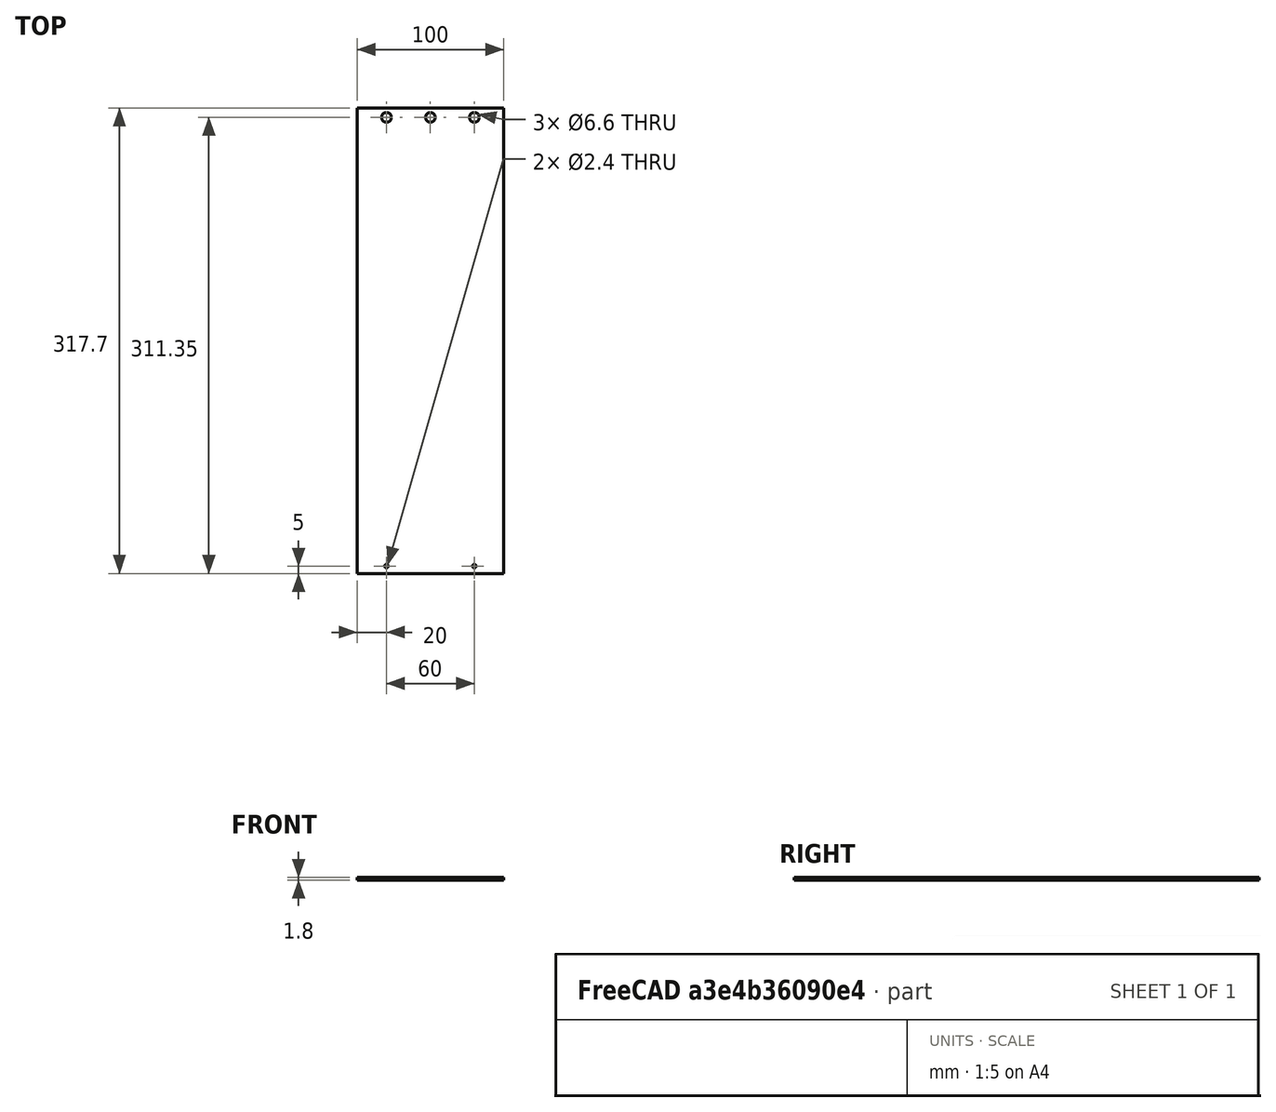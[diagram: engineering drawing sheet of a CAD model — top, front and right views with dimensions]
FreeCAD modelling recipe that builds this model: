
FCSTD DOCUMENT  (FreeCAD 0.20R29603 (Git))
Label: MechanicalCF35Mount004
License: All rights reserved
LicenseURL: http://en.wikipedia.org/wiki/All_rights_reserved
objects: Part::Cylinder×14, Part::Compound×10, TechDraw::DrawViewDimension×8, TechDraw::DrawProjGroupItem×2, Part::Box×1, Part::Cut×1, Part::Feature×1, TechDraw::DrawSVGTemplate×1, TechDraw::DrawProjGroup×1, TechDraw::DrawPage×1
note: 27 computed .brp shape members not serialized (recipe doc carries the construction recipe); baked Part::Feature solids carry a one-line shape summary decoded from their .brp

FEATURE [Part::Box] Box  label="Würfel"
  AttacherType = Attacher::AttachEngine3D
  Height = 1.8
  Length = 100
  Placement = pos=(-50,-305,50) rot=(0,0,1;0rad)
  Width = 317.7
FEATURE [Part::Cylinder] Cylinder  label="Zylinder"
  Angle = 360
  AttacherType = Attacher::AttachEngine3D
  FirstAngle = 0
  Height = 20
  Placement = pos=(30,2,40) rot=(0,0,1;0rad)
  Radius = 1.2
  SecondAngle = 0
FEATURE [Part::Cylinder] Cylinder015  label="Zylinder015"
  Angle = 360
  AttacherType = Attacher::AttachEngine3D
  FirstAngle = 0
  Height = 20
  Placement = pos=(-30,2,40) rot=(0,0,1;0rad)
  Radius = 1.2
  SecondAngle = 0
FEATURE [Part::Compound] Compound
  Links = -> [Cylinder,Cylinder015]
FEATURE [Part::Cylinder] Cylinder016  label="Zylinder016"
  Angle = 360
  AttacherType = Attacher::AttachEngine3D
  FirstAngle = 0
  Height = 20
  Placement = pos=(30,2,40) rot=(0,0,1;0rad)
  Radius = 1.2
  SecondAngle = 0
FEATURE [Part::Cylinder] Cylinder017  label="Zylinder017"
  Angle = 360
  AttacherType = Attacher::AttachEngine3D
  FirstAngle = 0
  Height = 20
  Placement = pos=(-30,2,40) rot=(0,0,1;0rad)
  Radius = 1.2
  SecondAngle = 0
FEATURE [Part::Compound] Compound015
  Links = -> [Cylinder016,Cylinder017]
  Placement = pos=(0,0,0) rot=(0,1,0;1.5708rad)
FEATURE [Part::Cylinder] Cylinder018  label="Zylinder018"
  Angle = 360
  AttacherType = Attacher::AttachEngine3D
  FirstAngle = 0
  Height = 20
  Placement = pos=(30,2,40) rot=(0,0,1;0rad)
  Radius = 1.2
  SecondAngle = 0
FEATURE [Part::Cylinder] Cylinder019  label="Zylinder019"
  Angle = 360
  AttacherType = Attacher::AttachEngine3D
  FirstAngle = 0
  Height = 20
  Placement = pos=(-30,2,40) rot=(0,0,1;0rad)
  Radius = 1.2
  SecondAngle = 0
FEATURE [Part::Compound] Compound016
  Links = -> [Cylinder018,Cylinder019]
  Placement = pos=(0,0,0) rot=(0,1,0;3.14159rad)
FEATURE [Part::Cylinder] Cylinder020  label="Zylinder020"
  Angle = 360
  AttacherType = Attacher::AttachEngine3D
  FirstAngle = 0
  Height = 20
  Placement = pos=(30,2,40) rot=(0,0,1;0rad)
  Radius = 1.2
  SecondAngle = 0
FEATURE [Part::Cylinder] Cylinder021  label="Zylinder021"
  Angle = 360
  AttacherType = Attacher::AttachEngine3D
  FirstAngle = 0
  Height = 20
  Placement = pos=(-30,2,40) rot=(0,0,1;0rad)
  Radius = 1.2
  SecondAngle = 0
FEATURE [Part::Compound] Compound017
  Links = -> [Cylinder020,Cylinder021]
  Placement = pos=(0,0,0) rot=(0,-1,0;1.5708rad)
FEATURE [Part::Compound] Compound018  label="M2Corehole"
  Links = -> [Compound017,Compound,Compound015,Compound016]
  Placement = pos=(0,-302,0) rot=(0,0,1;0rad)
FEATURE [Part::Cylinder] Cylinder004  label="Zylinder004"
  Angle = 360
  AttacherType = Attacher::AttachEngine3D
  FirstAngle = 0
  Height = 200
  Placement = pos=(30,6.35,-100) rot=(0,0,1;0rad)
  Radius = 3.3
  SecondAngle = 0
FEATURE [Part::Cylinder] Cylinder005  label="Zylinder005"
  Angle = 360
  AttacherType = Attacher::AttachEngine3D
  FirstAngle = 0
  Height = 200
  Placement = pos=(-30,6.35,-100) rot=(0,0,1;0rad)
  Radius = 3.3
  SecondAngle = 0
FEATURE [Part::Cylinder] Cylinder006  label="Zylinder006"
  Angle = 360
  AttacherType = Attacher::AttachEngine3D
  FirstAngle = 0
  Height = 200
  Placement = pos=(-30,6.35,-100) rot=(0,0,1;0rad)
  Radius = 3.3
  SecondAngle = 0
FEATURE [Part::Cylinder] Cylinder007  label="Zylinder007"
  Angle = 360
  AttacherType = Attacher::AttachEngine3D
  FirstAngle = 0
  Height = 200
  Placement = pos=(30,6.35,-100) rot=(0,0,1;0rad)
  Radius = 3.3
  SecondAngle = 0
FEATURE [Part::Compound] Compound004
  Links = -> [Cylinder006,Cylinder007]
  Placement = pos=(0,0,0) rot=(0,1,0;1.5708rad)
FEATURE [Part::Compound] Compound005
  Links = -> [Cylinder004,Cylinder005,Compound004]
FEATURE [Part::Cylinder] Cylinder008  label="Zylinder008"
  Angle = 360
  AttacherType = Attacher::AttachEngine3D
  FirstAngle = 0
  Height = 200
  Placement = pos=(0,6.35,-100) rot=(0,0,1;0rad)
  Radius = 3.3
  SecondAngle = 0
FEATURE [Part::Cylinder] Cylinder009  label="Zylinder009"
  Angle = 360
  AttacherType = Attacher::AttachEngine3D
  FirstAngle = 0
  Height = 200
  Placement = pos=(0,6.35,-100) rot=(0,0,1;0rad)
  Radius = 3.3
  SecondAngle = 0
FEATURE [Part::Compound] Compound007
  Links = -> [Cylinder009]
  Placement = pos=(0,0,0) rot=(0,1,0;1.5708rad)
FEATURE [Part::Compound] Compound008
  Links = -> [Compound005,Cylinder008,Compound007]
FEATURE [Part::Compound] Compound019
  Links = -> [Compound018,Compound008]
FEATURE [Part::Cut] Cut
  Base = -> Box
  Tool = -> Compound019
FEATURE [Part::Feature] Cut_solid  label="Cut (Solid)"
  shape: bbox 100 x 317.7 x 1.8 mm, 11 faces (baked)
FEATURE [TechDraw::DrawSVGTemplate] Template
  EditableTexts = Designed_by_Name=Thoams Spielauer; FC-Date=2023-07-05; FC-SC=mm; FC-SH=01; FC-Title=CF40 electronics housing; Subtitle=Bottom sheet
  Height = 210
  Orientation = 1
  Width = 297
FEATURE [TechDraw::DrawProjGroupItem] ProjItem  label="Front"
  CoarseView = false
  Direction = (0,0,1)
  Focus = 100
  HardHidden = false
  IsoCount = 0
  IsoHidden = false
  IsoVisible = false
  LockPosition = true
  Perspective = false
  Rotation = 0
  RotationVector = (1,0,0)
  Scale = 0.333333
  ScaleType = 2
  SeamHidden = false
  SeamVisible = true
  SmoothHidden = false
  SmoothVisible = true
  Source = -> [Cut_solid]
  Type = 0
  X = 0
  XDirection = (1,0,0)
  Y = 0
FEATURE [TechDraw::DrawProjGroupItem] ProjItem001  label="Left"
  CoarseView = false
  Direction = (-1,0,1e-16)
  Focus = 100
  HardHidden = false
  IsoCount = 0
  IsoHidden = false
  IsoVisible = false
  LockPosition = false
  Perspective = false
  Rotation = 0
  RotationVector = (1,0,0)
  ScaleType = 2
  SeamHidden = false
  SeamVisible = true
  SmoothHidden = false
  SmoothVisible = true
  Source = -> [Cut_solid]
  Type = 1
  X = 48.3333
  XDirection = (1e-16,0,1)
  Y = 0
FEATURE [TechDraw::DrawProjGroup] ProjGroup
  Anchor = -> ProjItem
  AutoDistribute = true
  LockPosition = false
  ProjectionType = 0
  Rotation = 0
  Scale = 0.333333
  ScaleType = 2
  Source = -> [Cut_solid]
  Views = -> [ProjItem,ProjItem001]
  X = 87.4123
  Y = 128.335
  spacingX = 15
  spacingY = 15
FEATURE [TechDraw::DrawViewDimension] Dimension
  AngleOverride = false
  Arbitrary = false
  ArbitraryTolerances = false
  EqualTolerance = true
  ExtensionAngle = 0
  FormatSpec = %.2w
  FormatSpecOverTolerance = %+.2w
  FormatSpecUnderTolerance = %+.2w
  Inverted = false
  LineAngle = 0
  LockPosition = false
  MeasureType = 1
  OverTolerance = 0
  References2D = -> [ProjItem]
  Rotation = 0
  ScaleType = 0
  TheoreticalExact = false
  Type = 0
  UnderTolerance = 0
  X = -33.2555
  Y = 1.26203
FEATURE [TechDraw::DrawViewDimension] Dimension001
  AngleOverride = false
  Arbitrary = false
  ArbitraryTolerances = false
  EqualTolerance = true
  ExtensionAngle = 0
  FormatSpec = %.2w
  FormatSpecOverTolerance = %+.2w
  FormatSpecUnderTolerance = %+.2w
  Inverted = false
  LineAngle = 0
  LockPosition = false
  MeasureType = 1
  OverTolerance = 0
  References2D = -> [ProjItem]
  Rotation = 0
  ScaleType = 0
  TheoreticalExact = false
  Type = 0
  UnderTolerance = 0
  X = -1.23797
  Y = -66.7912
FEATURE [TechDraw::DrawViewDimension] Dimension002
  AngleOverride = false
  Arbitrary = false
  ArbitraryTolerances = false
  EqualTolerance = true
  ExtensionAngle = 0
  FormatSpec = %.2w
  FormatSpecOverTolerance = %+.2w
  FormatSpecUnderTolerance = %+.2w
  Inverted = false
  LineAngle = 0
  LockPosition = false
  MeasureType = 1
  OverTolerance = 0
  References2D = -> [ProjItem001]
  Rotation = 0
  ScaleType = 0
  TheoreticalExact = false
  Type = 0
  UnderTolerance = 0
  X = 0.102835
  Y = 63.4252
FEATURE [TechDraw::DrawViewDimension] Dimension003
  AngleOverride = false
  Arbitrary = false
  ArbitraryTolerances = false
  EqualTolerance = true
  ExtensionAngle = 0
  FormatSpec = %.2w
  FormatSpecOverTolerance = %+.2w
  FormatSpecUnderTolerance = %+.2w
  Inverted = false
  LineAngle = 0
  LockPosition = false
  MeasureType = 1
  OverTolerance = 0
  References2D = -> [ProjItem]
  Rotation = 0
  ScaleType = 0
  TheoreticalExact = false
  Type = 0
  UnderTolerance = 0
  X = 7.70254
  Y = 64.3208
FEATURE [TechDraw::DrawViewDimension] Dimension004
  AngleOverride = false
  Arbitrary = false
  ArbitraryTolerances = false
  EqualTolerance = true
  ExtensionAngle = 0
  FormatSpec = %.2w
  FormatSpecOverTolerance = %+.2w
  FormatSpecUnderTolerance = %+.2w
  Inverted = false
  LineAngle = 0
  LockPosition = false
  MeasureType = 1
  OverTolerance = 0
  References2D = -> [ProjItem]
  Rotation = 0
  ScaleType = 0
  TheoreticalExact = false
  Type = 0
  UnderTolerance = 0
  X = -12.2736
  Y = 64.3062
FEATURE [TechDraw::DrawViewDimension] Dimension005
  AngleOverride = false
  Arbitrary = false
  ArbitraryTolerances = false
  EqualTolerance = true
  ExtensionAngle = 0
  FormatSpec = ⌀%.2w (3x)
  FormatSpecOverTolerance = %+.2w
  FormatSpecUnderTolerance = %+.2w
  Inverted = false
  LineAngle = 0
  LockPosition = false
  MeasureType = 1
  OverTolerance = 0
  References2D = -> [ProjItem]
  Rotation = 0
  ScaleType = 0
  TheoreticalExact = false
  Type = 5
  UnderTolerance = 0
  X = 1.44604
  Y = 36.618
FEATURE [TechDraw::DrawViewDimension] Dimension006
  AngleOverride = false
  Arbitrary = false
  ArbitraryTolerances = false
  EqualTolerance = true
  ExtensionAngle = 0
  FormatSpec = %.2w
  FormatSpecOverTolerance = %+.2w
  FormatSpecUnderTolerance = %+.2w
  Inverted = false
  LineAngle = 0
  LockPosition = false
  MeasureType = 1
  OverTolerance = 0
  References2D = -> [ProjItem]
  Rotation = 0
  ScaleType = 0
  TheoreticalExact = false
  Type = 0
  UnderTolerance = 0
  X = 12.0421
  Y = -78.1672
FEATURE [TechDraw::DrawViewDimension] Dimension007
  AngleOverride = false
  Arbitrary = false
  ArbitraryTolerances = false
  EqualTolerance = true
  ExtensionAngle = 0
  FormatSpec = ⌀%.2w (2x)
  FormatSpecOverTolerance = %+.2w
  FormatSpecUnderTolerance = %+.2w
  Inverted = false
  LineAngle = 0
  LockPosition = false
  MeasureType = 1
  OverTolerance = 0
  References2D = -> [ProjItem]
  Rotation = 0
  ScaleType = 0
  TheoreticalExact = false
  Type = 5
  UnderTolerance = 0
  X = -9.25376
  Y = -35.5101
FEATURE [TechDraw::DrawPage] Page
  KeepUpdated = true
  NextBalloonIndex = 1
  ProjectionType = 0
  Template = -> Template
  Views = -> [ProjGroup,Dimension,Dimension001,Dimension002,Dimension003,Dimension004,Dimension005,Dimension006,Dimension007]
